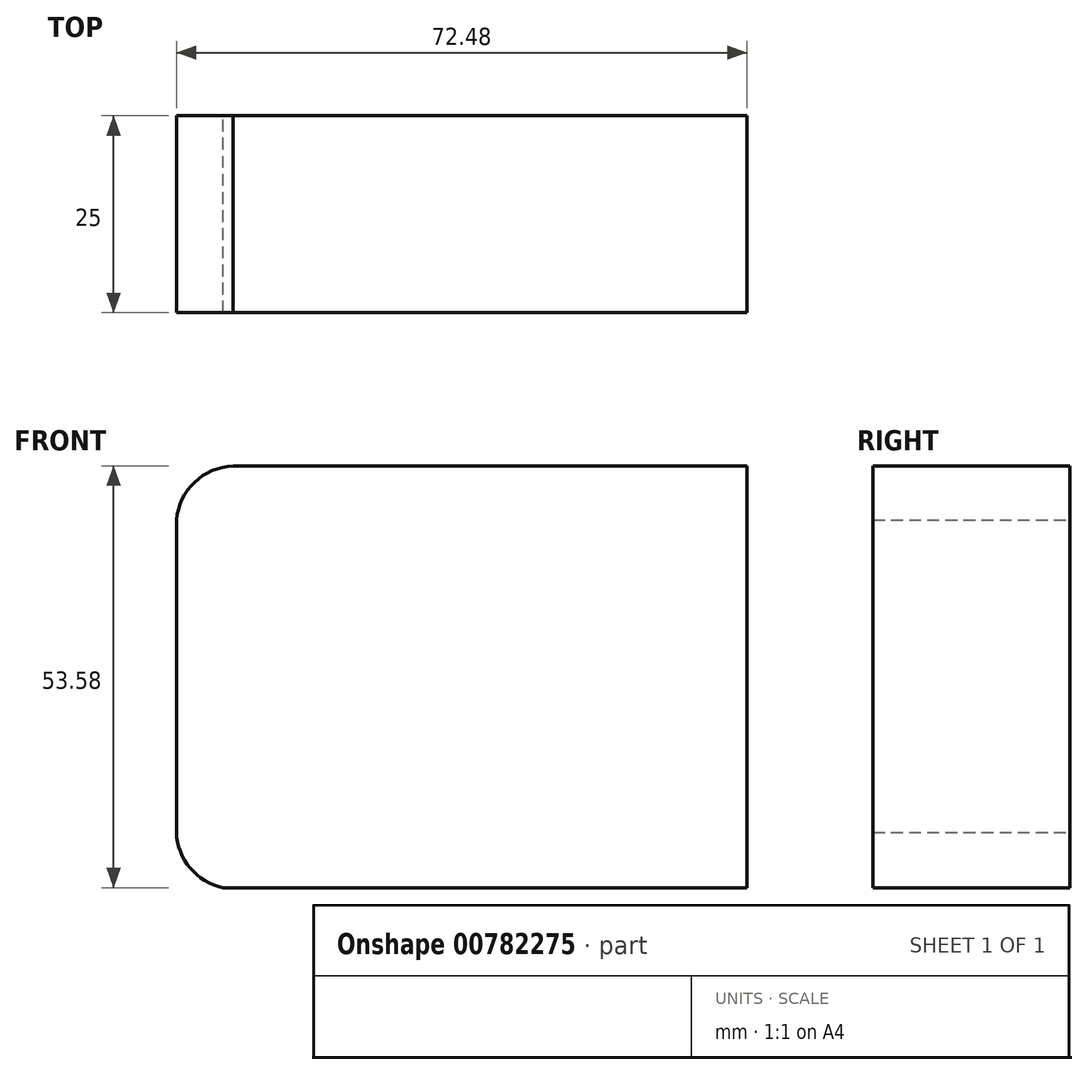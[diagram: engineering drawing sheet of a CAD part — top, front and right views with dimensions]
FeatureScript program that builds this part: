
annotation { "Feature Type Name" : "Feature", "Feature Type Description" : "" }
export const myFeature = defineFeature(function(context is Context, id is Id, definition is map)
    precondition{}
    {
        {
            var Q0;
            Q0=qCreatedBy(makeId("Front.planeOp"),FACE);
            var sketch = newSketch(context, id + "F0", { "sketchPlane" : qUnion([Q0])});
            skLineSegment(sketch, "E0.bottom", {"start": v(0, 0) * mm, "end": v(72.48, 0) * mm});
            skLineSegment(sketch, "E0.top", {"start": v(0, 53.58) * mm, "end": v(72.48, 53.58) * mm});
            skLineSegment(sketch, "E0.left", {"start": v(0, 0) * mm, "end": v(0, 53.58) * mm});
            skLineSegment(sketch, "E0.right", {"start": v(72.48, 0) * mm, "end": v(72.48, 53.58) * mm});
            skArc(sketch, "E1", {"start": v(7.72, 53.58) * mm, "mid": v(2.04, 51.25) * mm, "end": v(0, 45.46) * mm});
            skArc(sketch, "E2", {"start": v(0, 7.05) * mm, "mid": v(2.9, 1.4) * mm, "end": v(9.1, 0) * mm});
            skLineSegment(sketch, "E3", {"start": v(7.47, 46.08) * mm, "end": v(7.5, 7.33) * mm});
            skSolve(sketch);
        }
        {
            var Q0;
            Q0=makeQuery(id+"F0.imprint","IMPRINT",FACE,{"disambiguationData":[TD([[makeQuery(id+"F0.imprint","IMPRINT",EDGE,{"derivedFrom":sQuery(id+"F0.wireOp",EDGE,"E0.bottom")}),1.0]])]});
            extrude(context, id + "F1", {"entities" : qUnion([Q0]), "depth" : 25 * mm, "offsetDistance" : 25 * mm});
        }
    });
